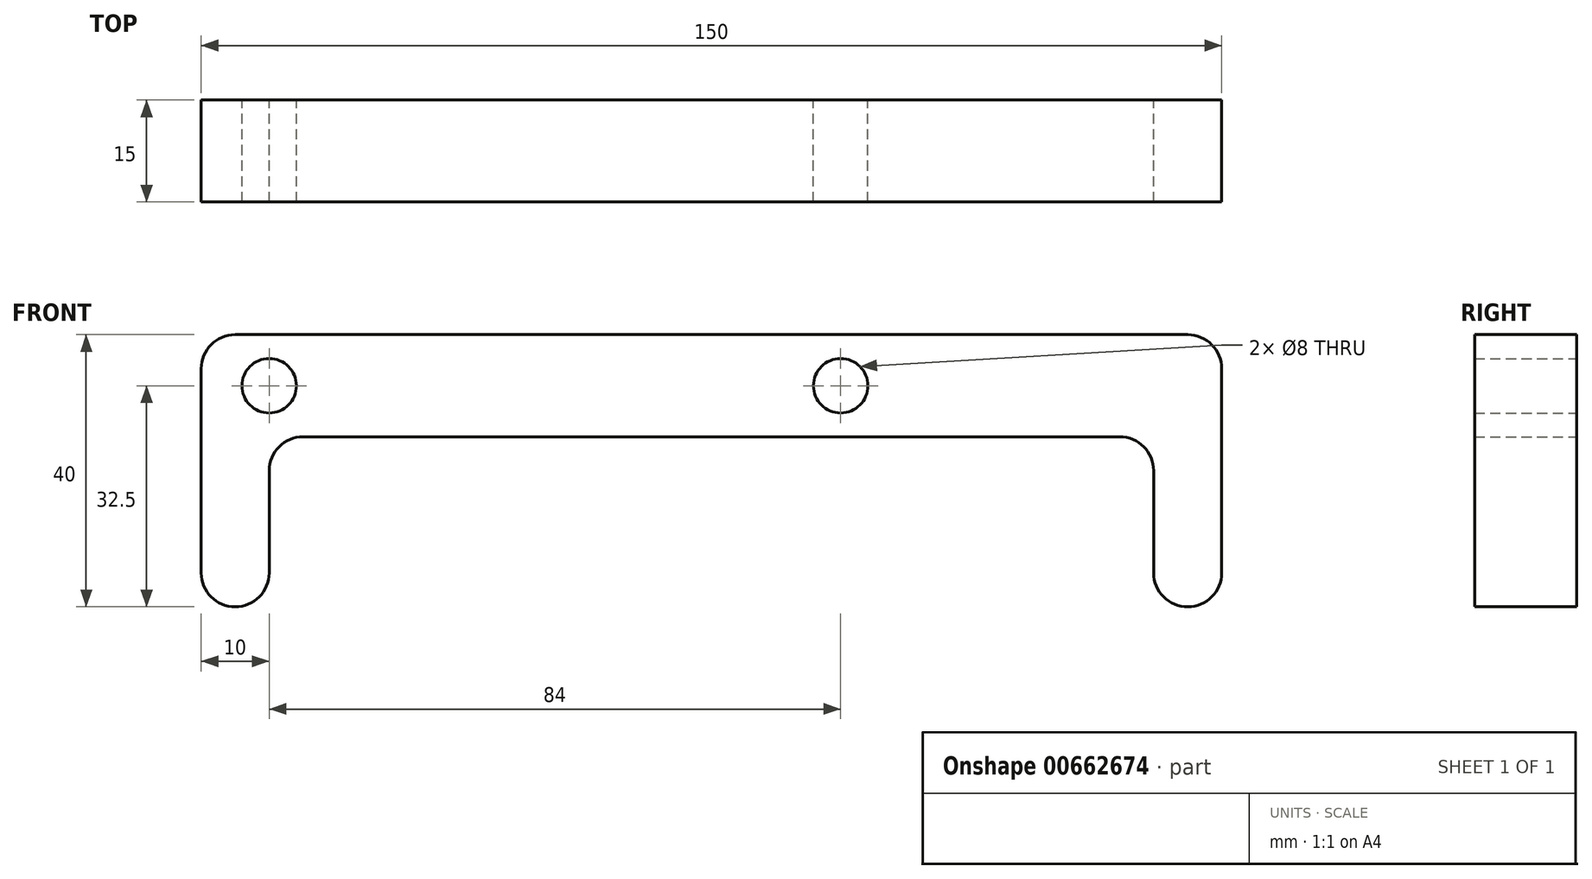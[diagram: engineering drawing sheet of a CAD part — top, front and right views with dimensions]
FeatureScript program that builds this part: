
annotation { "Feature Type Name" : "Feature", "Feature Type Description" : "" }
export const myFeature = defineFeature(function(context is Context, id is Id, definition is map)
    precondition{}
    {
        {
            var Q0;
            Q0=qCreatedBy(makeId("Front.planeOp"),FACE);
            var sketch = newSketch(context, id + "F0", { "sketchPlane" : qUnion([Q0])});
            skCircle(sketch, "E0", {"center": v(0, 0) * mm, "radius": 4 * mm});
            skCircle(sketch, "E1", {"center": v(-84, 0) * mm, "radius": 4 * mm});
            skLineSegment(sketch, "E2.bottom", {"start": v(-94, 7.5) * mm, "end": v(56, 7.5) * mm});
            skLineSegment(sketch, "E2.top", {"start": v(-94, -7.5) * mm, "end": v(56, -7.5) * mm});
            skLineSegment(sketch, "E2.left", {"start": v(-94, 7.5) * mm, "end": v(-94, -7.5) * mm});
            skLineSegment(sketch, "E2.right", {"start": v(56, 7.5) * mm, "end": v(56, -7.5) * mm});
            skLineSegment(sketch, "E3.bottom", {"start": v(-94, -7.5) * mm, "end": v(-84, -7.5) * mm});
            skLineSegment(sketch, "E3.top", {"start": v(-94, -32.5) * mm, "end": v(-84, -32.5) * mm});
            skLineSegment(sketch, "E3.left", {"start": v(-94, -7.5) * mm, "end": v(-94, -32.5) * mm});
            skLineSegment(sketch, "E3.right", {"start": v(-84, -7.5) * mm, "end": v(-84, -32.5) * mm});
            skLineSegment(sketch, "E4.bottom", {"start": v(56, -7.5) * mm, "end": v(46, -7.5) * mm});
            skLineSegment(sketch, "E4.top", {"start": v(56, -32.5) * mm, "end": v(46, -32.5) * mm});
            skLineSegment(sketch, "E4.left", {"start": v(56, -7.5) * mm, "end": v(56, -32.5) * mm});
            skLineSegment(sketch, "E4.right", {"start": v(46, -7.5) * mm, "end": v(46, -32.5) * mm});
            skSolve(sketch);
        }
        {
            var Q0;
            Q0=qSketchRegion(id+"F0",true);
            extrude(context, id + "F1", {"entities" : qUnion([Q0]), "depth" : 15 * mm});
        }
        {
            var Q0;
            Q0=makeQuery(id+"F1.opExtrude","SWEPT_EDGE",EDGE,{"disambiguationData":[OSD([sQuery(id+"F0.wireOp",EDGE,"E2.top"),sQuery(id+"F0.wireOp",EDGE,"E3.bottom"),sQuery(id+"F0.wireOp",EDGE,"E3.right")])]});
            var Q1;
            Q1=makeQuery(id+"F1.opExtrude","SWEPT_EDGE",EDGE,{"disambiguationData":[OSD([sQuery(id+"F0.wireOp",EDGE,"E2.top"),sQuery(id+"F0.wireOp",EDGE,"E4.bottom"),sQuery(id+"F0.wireOp",EDGE,"E4.right")])]});
            var Q2;
            Q2=makeQuery(id+"F1.opExtrude","SWEPT_EDGE",EDGE,{"disambiguationData":[OSD([sQuery(id+"F0.wireOp",EDGE,"E2.bottom"),sQuery(id+"F0.wireOp",EDGE,"E2.right")])]});
            var Q3;
            Q3=makeQuery(id+"F1.opExtrude","SWEPT_EDGE",EDGE,{"disambiguationData":[OSD([sQuery(id+"F0.wireOp",EDGE,"E4.top"),sQuery(id+"F0.wireOp",EDGE,"E4.left")])]});
            var Q4;
            Q4=makeQuery(id+"F1.opExtrude","SWEPT_EDGE",EDGE,{"disambiguationData":[OSD([sQuery(id+"F0.wireOp",EDGE,"E4.top"),sQuery(id+"F0.wireOp",EDGE,"E4.right")])]});
            var Q5;
            Q5=makeQuery(id+"F1.opExtrude","SWEPT_EDGE",EDGE,{"disambiguationData":[OSD([sQuery(id+"F0.wireOp",EDGE,"E3.top"),sQuery(id+"F0.wireOp",EDGE,"E3.left")])]});
            var Q6;
            Q6=makeQuery(id+"F1.opExtrude","SWEPT_EDGE",EDGE,{"disambiguationData":[OSD([sQuery(id+"F0.wireOp",EDGE,"E3.top"),sQuery(id+"F0.wireOp",EDGE,"E3.right")])]});
            var Q7;
            Q7=makeQuery(id+"F1.opExtrude","SWEPT_EDGE",EDGE,{"disambiguationData":[OSD([sQuery(id+"F0.wireOp",EDGE,"E2.bottom"),sQuery(id+"F0.wireOp",EDGE,"E2.left")])]});
            fillet(context, id + "F2", {"entities" : qUnion([Q0, Q1, Q2, Q3, Q4, Q5, Q6, Q7]), "radius" : 5 * mm, "tangentPropagation" : true, "allowEdgeOverflow" : false});
        }
    });
